# Revit family: Shower-Bath_Shower-STERLING-Accord-71240123_1
name_source: partatom
category: Plumbing Fixtures
revit_build: Autodesk Revit 2015 (Build: 20140606_1530(x64)
units: mm (PartAtom-declared; Revit-internal decimal feet)

## types (4) — shared parameters
ADA Compliant = No
Assembly Code = D2010500
CW Connection = No
Cold Water Inlet = Cold Water Inlet
Date Modified = 7/22/2019
Default Elevation = 0"
Description = 60 inch bath/shower with Aging in Place grab bars
Drain Included = No
HW Connection = No
Height = 73 1/4"
Hot Water Inlet = Hot Water Inlet
Length = 60"
Manufacturer = KOHLER Co.
MasterFormat 1995 = 15410
MasterFormat 2004 = 22.41.19
Material = Solid Vikrell
Product Documentation Link = https://resources.kohler.com
Product Name = Accord
Product Page URL = https://www.sterlingplumbing.com
URL = https://www.sterlingplumbing.com
Vent Connection = No
Waste Connection = Yes
Waste Water Outlet = Waste Water Outlet
WaterSense Certified = No
Width = 31 1/4"

## per-type parameters (varying)
| type | Finish | Grab Bar Material | Model | Type |
| Matte Silver Grab Bar, 0-White | Sterling-Vikrell-0-White | Sterling-Metal-V-Matte_Silver | 71240123-V-0 | 1 |
| Matte Silver Grab Bar, 96-Biscuit | Sterling-Vikrell-96-Biscuit | Sterling-Metal-V-Matte_Silver | 71240123-V-96 | 2 |
| Nickel Grab Bar, 96-Biscuit | Sterling-Vikrell-96-Biscuit | Sterling-Metal-N-Nickel | 71240123-N-96 | 3 |
| Nickel Grab Bar, 0-White | Sterling-Vikrell-0-White | Sterling-Metal-N-Nickel | 71240123-N-0 | 4 |

## geometry (parser evidence)
native form markers: Sweep x6
no freeform markers — native parametric forms only
